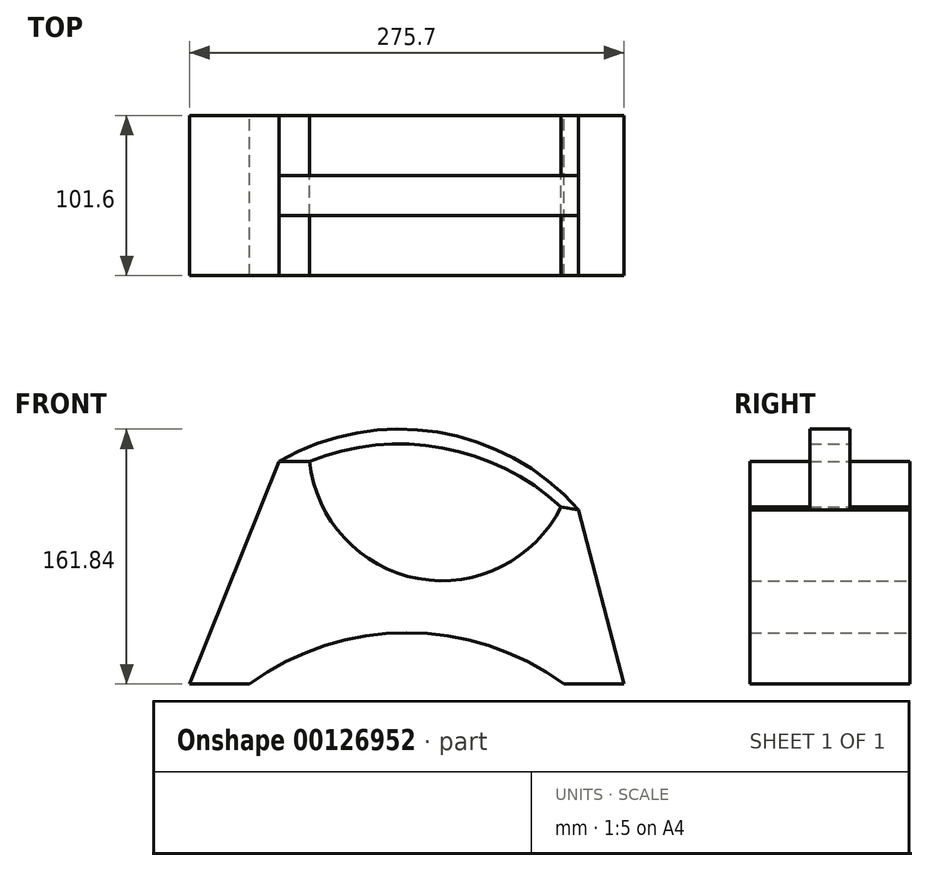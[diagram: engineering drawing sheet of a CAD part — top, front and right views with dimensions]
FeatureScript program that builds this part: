
annotation { "Feature Type Name" : "Feature", "Feature Type Description" : "" }
export const myFeature = defineFeature(function(context is Context, id is Id, definition is map)
    precondition{}
    {
        {
            var Q0;
            Q0=qCreatedBy(makeId("Front.planeOp"),FACE);
            var sketch = newSketch(context, id + "F0", { "sketchPlane" : qUnion([Q0])});
            skLineSegment(sketch, "E0.bottom", {"start": v(-76.2, 141.43) * mm, "end": v(-56.78, 141.43) * mm});
            skPoint(sketch, "E1.center.orphan", {"position": v(0, 0) * mm});
            skLineSegment(sketch, "E2", {"start": v(102.9, 112.42) * mm, "end": v(113.96, 110.63) * mm});
            skArc(sketch, "E3.trimOffspring", {"start": v(102.9, 112.42) * mm, "mid": v(27.24, 149.95) * mm, "end": v(-56.78, 141.43) * mm});
            skArc(sketch, "E4.trimOffspring", {"start": v(113.96, 110.63) * mm, "mid": v(24.37, 159.88) * mm, "end": v(-76.2, 141.43) * mm});
            skSolve(sketch);
        }
        {
            var Q0;
            Q0 = qSketchRegion(id + "F0", true);
            extrude(context, id + "F1", {"entities" : qUnion([Q0]), "depth" : 12.7 * mm, "hasSecondDirection" : true, "secondDirectionOppositeDirection" : true, "secondDirectionDepth" : 12.7 * mm});
        }
        {
            var Q0;
            Q0=qCreatedBy(makeId("Front.planeOp"),FACE);
            var sketch = newSketch(context, id + "F2", { "sketchPlane" : qUnion([Q0])});
            skArc(sketch, "E5.0", {"start": v(102.9, 112.42) * mm, "mid": v(27.24, 149.95) * mm, "end": v(-56.78, 141.43) * mm});
            skLineSegment(sketch, "E6.0", {"start": v(-76.2, 141.43) * mm, "end": v(-56.78, 141.43) * mm});
            skLineSegment(sketch, "E7.0", {"start": v(102.9, 112.42) * mm, "end": v(113.96, 110.63) * mm});
            skArc(sketch, "E8", {"start": v(-56.78, 141.43) * mm, "mid": v(12.14, 66.85) * mm, "end": v(102.9, 112.42) * mm});
            skLineSegment(sketch, "E9", {"start": v(-76.2, 141.43) * mm, "end": v(-132.98, 0) * mm});
            skLineSegment(sketch, "E10", {"start": v(113.96, 110.63) * mm, "end": v(142.72, 0) * mm});
            skLineSegment(sketch, "E11", {"start": v(-132.98, 0) * mm, "end": v(-94.88, 0) * mm});
            skLineSegment(sketch, "E12", {"start": v(142.72, 0) * mm, "end": v(104.62, 0) * mm});
            skArc(sketch, "E13", {"start": v(104.62, 0) * mm, "mid": v(4.87, 32.42) * mm, "end": v(-94.88, 0) * mm});
            skSolve(sketch);
        }
        {
            var Q0;
            Q0=makeQuery(id+"F2.imprint","IMPRINT",FACE,{"disambiguationData":[TD([[makeQuery(id+"F2.imprint","IMPRINT",EDGE,{"derivedFrom":sQuery(id+"F2.wireOp",EDGE,"E6.0")}),-1.0]])]});
            extrude(context, id + "F3", {"entities" : qUnion([Q0]), "operationType" : NewBodyOperationType.ADD, "depth" : 50.8 * mm, "hasSecondDirection" : true, "secondDirectionOppositeDirection" : true, "secondDirectionDepth" : 50.8 * mm});
        }
    });
